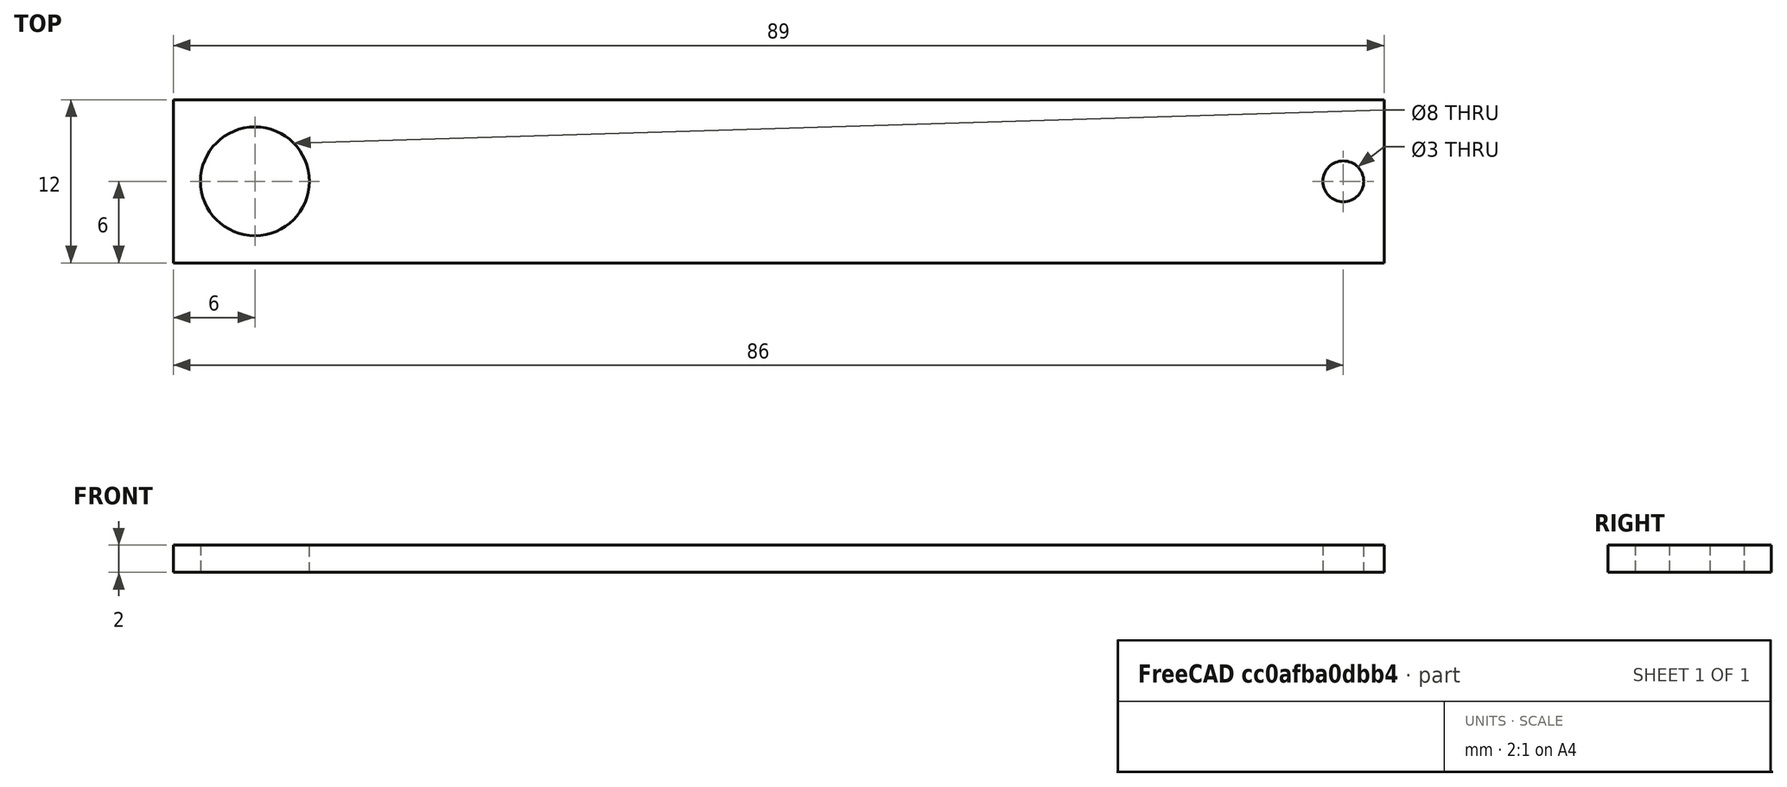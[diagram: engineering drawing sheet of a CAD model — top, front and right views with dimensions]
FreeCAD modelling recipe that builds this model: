
FCSTD DOCUMENT  (FreeCAD 0.19R24276 (Git))
Label: richag_80_1
License: All rights reserved
LicenseURL: http://en.wikipedia.org/wiki/All_rights_reserved
objects: Sketcher::SketchObject×1, PartDesign::Pad×1, PartDesign::Body×1
note: 4 computed .brp shape members not serialized (recipe doc carries the construction recipe); baked Part::Feature solids carry a one-line shape summary decoded from their .brp

FEATURE [Sketcher::SketchObject] Sketch
  FullyConstrained = false
  MapMode = 5
  Support = -> [XY_Plane]
  sketch-geometry (6):
    g0: Circle CenterX=0 CenterY=0 CenterZ=0 NormalX=0 NormalY=0 NormalZ=1 AngleXU=0 Radius=4
    g1: Circle CenterX=80 CenterY=0 CenterZ=0 NormalX=0 NormalY=0 NormalZ=1 AngleXU=0 Radius=1.5
    g2: LineSegment StartX=-6 StartY=-6 StartZ=0 EndX=83 EndY=-6 EndZ=0
    g3: LineSegment StartX=83 StartY=-6 StartZ=0 EndX=83 EndY=6 EndZ=0
    g4: LineSegment StartX=83 StartY=6 StartZ=0 EndX=-6 EndY=6 EndZ=0
    g5: LineSegment StartX=-6 StartY=6 StartZ=0 EndX=-6 EndY=-6 EndZ=0
  constraints (15):
    c: PointOnObject(g1,g-1)
    c: Diameter(g1) = 3
    c: Diameter(g0) = 8
    c: Coincident(g2,g3)
    c: Coincident(g3,g4)
    c: Coincident(g4,g5)
    c: Coincident(g5,g2)
    c: Horizontal(g2)
    c: Horizontal(g4)
    c: Vertical(g3)
    c: Vertical(g5)
    c: DistanceX(g2,g-1) = 6
    c: DistanceX(g1,g3) = 3
    c: DistanceY(g2,g-1) = 6
    c: DistanceY(g-1,g4) = 6
FEATURE [PartDesign::Pad] Pad
  Direction = (1,1,1)
  Length = 2
  Length2 = 100
  Profile = -> Sketch
  Type = 0
FEATURE [PartDesign::Body] Body
  Group = -> [Sketch,Pad]
  Origin = -> Origin
  Tip = -> Pad
